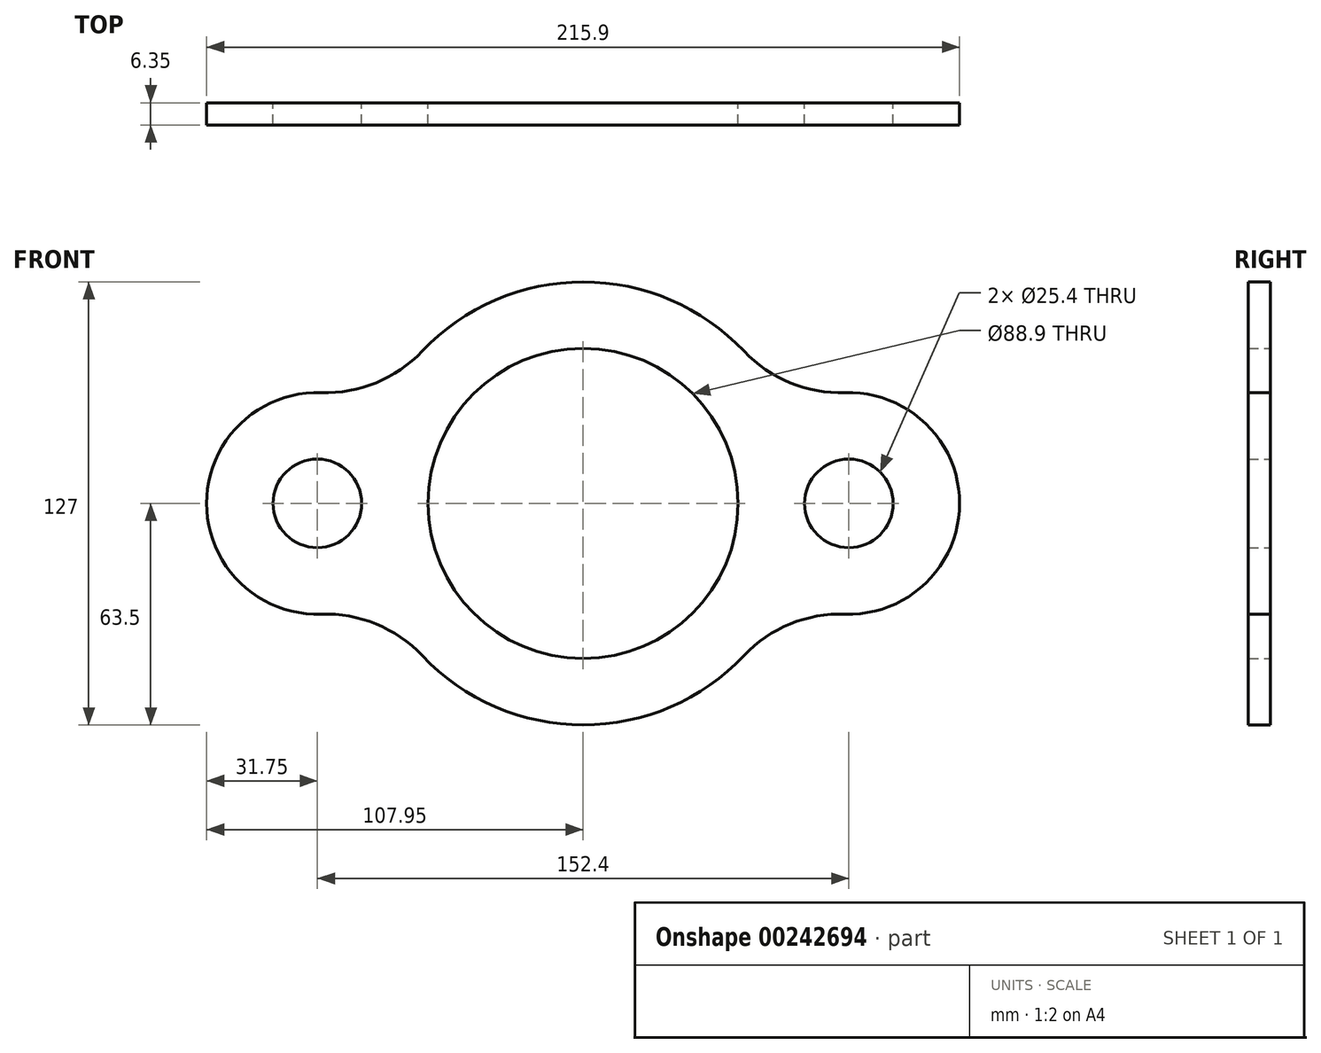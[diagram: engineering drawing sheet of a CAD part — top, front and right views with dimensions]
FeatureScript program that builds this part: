
annotation { "Feature Type Name" : "Feature", "Feature Type Description" : "" }
export const myFeature = defineFeature(function(context is Context, id is Id, definition is map)
    precondition{}
    {
        {
            var Q0;
            Q0=qCreatedBy(makeId("Front.planeOp"),FACE);
            var sketch = newSketch(context, id + "F0", { "sketchPlane" : qUnion([Q0])});
            skArc(sketch, "E0", {"start": v(46.14, 43.63) * mm, "mid": v(0, 63.5) * mm, "end": v(-46.14, 43.63) * mm});
            skCircle(sketch, "E1", {"center": v(0, 0) * mm, "radius": 44.45 * mm});
            skArc(sketch, "E2", {"start": v(75.12, -31.73) * mm, "mid": v(107.95, 0) * mm, "end": v(75.12, 31.73) * mm});
            skCircle(sketch, "E3", {"center": v(76.2, 0) * mm, "radius": 12.7 * mm});
            skArc(sketch, "E4", {"start": v(-75.12, 31.73) * mm, "mid": v(-107.95, 0) * mm, "end": v(-75.12, -31.73) * mm});
            skCircle(sketch, "E5", {"center": v(-76.2, 0) * mm, "radius": 12.7 * mm});
            skArc(sketch, "E6.trimOffspring", {"start": v(-46.14, -43.63) * mm, "mid": v(0, -63.5) * mm, "end": v(46.14, -43.63) * mm});
            skPoint(sketch, "E7.visualSharp", {"position": v(57.94, 25.98) * mm});
            skArc(sketch, "E7.filletArc", {"start": v(46.14, 43.63) * mm, "mid": v(59.35, 34.56) * mm, "end": v(75.12, 31.73) * mm});
            skPoint(sketch, "E8.visualSharp", {"position": v(-57.94, 25.98) * mm});
            skArc(sketch, "E8.filletArc", {"start": v(-75.12, 31.73) * mm, "mid": v(-59.35, 34.56) * mm, "end": v(-46.14, 43.63) * mm});
            skPoint(sketch, "E9.visualSharp", {"position": v(-57.94, -25.98) * mm});
            skArc(sketch, "E9.filletArc", {"start": v(-46.14, -43.63) * mm, "mid": v(-59.35, -34.56) * mm, "end": v(-75.12, -31.73) * mm});
            skPoint(sketch, "E10.visualSharp", {"position": v(57.94, -25.98) * mm});
            skArc(sketch, "E10.filletArc", {"start": v(75.12, -31.73) * mm, "mid": v(59.35, -34.56) * mm, "end": v(46.14, -43.63) * mm});
            skSolve(sketch);
        }
        {
            var Q0;
            Q0=makeQuery(id+"F0.imprint","IMPRINT",FACE,{"disambiguationData":[TD([[makeQuery(id+"F0.imprint","IMPRINT",EDGE,{"derivedFrom":sQuery(id+"F0.wireOp",EDGE,"E0")}),1.0]])]});
            extrude(context, id + "F1", {"entities" : qUnion([Q0]), "depth" : 6.35 * mm});
        }
    });
